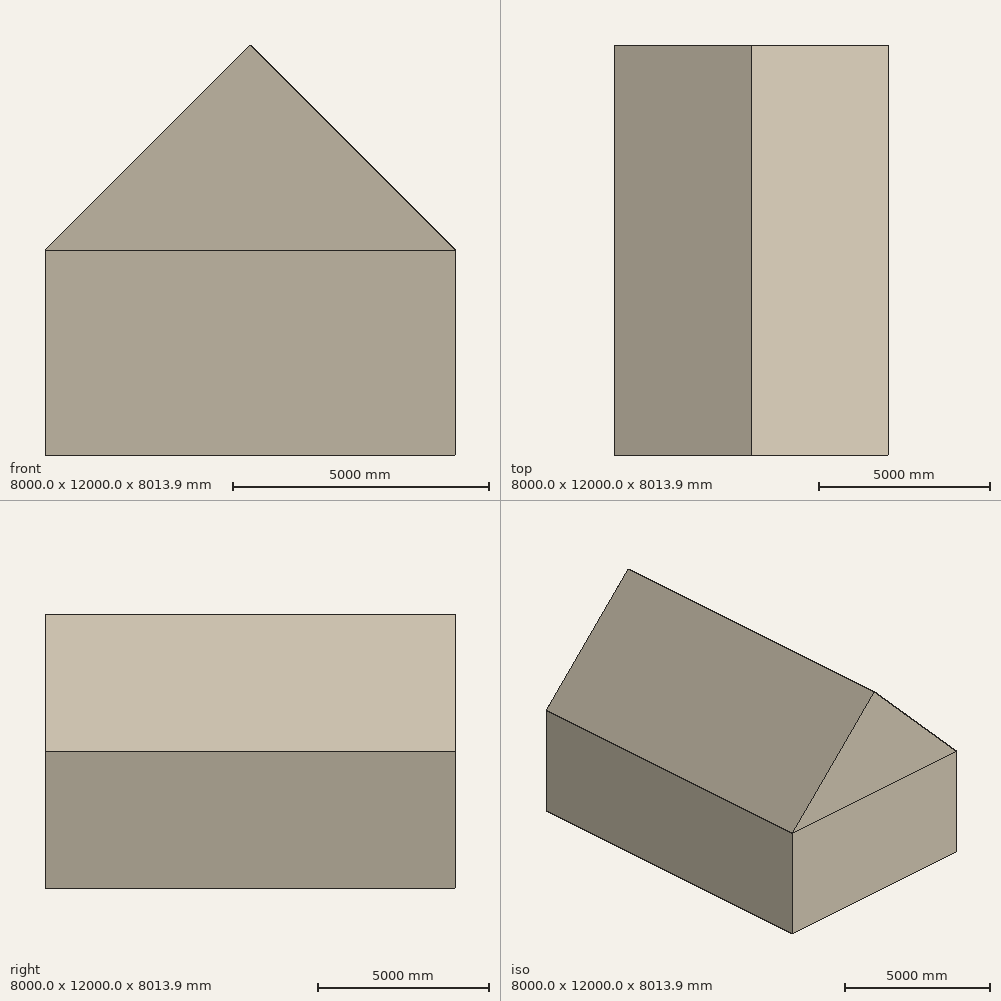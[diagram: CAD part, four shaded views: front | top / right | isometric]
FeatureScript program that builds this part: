
annotation { "Feature Type Name" : "Feature", "Feature Type Description" : "" }
export const myFeature = defineFeature(function(context is Context, id is Id, definition is map)
    precondition{}
    {
        {
            var Q0;
            Q0=qCreatedBy(makeId("Front.planeOp"),FACE);
            var sketch = newSketch(context, id + "F0", { "sketchPlane" : qUnion([Q0])});
            skLineSegment(sketch, "E0.bottom", {"start": v(0, 0) * mm, "end": v(8000, 0) * mm});
            skLineSegment(sketch, "E0.top", {"start": v(0, 4000) * mm, "end": v(8000, 4000) * mm});
            skLineSegment(sketch, "E0.left", {"start": v(0, 0) * mm, "end": v(0, 4000) * mm});
            skLineSegment(sketch, "E0.right", {"start": v(8000, 0) * mm, "end": v(8000, 4000) * mm});
            skSolve(sketch);
        }
        {
            var Q0;
            Q0 = qSketchRegion(id + "F0", true);
            extrude(context, id + "F1", {"entities" : qUnion([Q0]), "depth" : 12000 * mm});
        }
        {
            var Q0;
            Q0=qCreatedBy(makeId("Front.planeOp"),FACE);
            var sketch = newSketch(context, id + "F2", { "sketchPlane" : qUnion([Q0])});
            skLineSegment(sketch, "E1", {"start": v(0, 4013.9) * mm, "end": v(4000, 4013.9) * mm});
            skLineSegment(sketch, "E2", {"start": v(4000, 4013.9) * mm, "end": v(4000, 8013.9) * mm});
            skPoint(sketch, "E2.endSnap0", {"position": v(3969.53, 8013.9) * mm});
            skLineSegment(sketch, "E3", {"start": v(4000, 8013.9) * mm, "end": v(0, 4013.9) * mm});
            skLineSegment(sketch, "E4", {"start": v(4000, 8013.9) * mm, "end": v(8000, 4013.9) * mm});
            skLineSegment(sketch, "E5", {"start": v(8000, 4013.9) * mm, "end": v(4000, 4013.9) * mm});
            skSolve(sketch);
        }
        {
            var Q0;
            Q0=makeQuery(id+"F2.imprint","IMPRINT",FACE,{"disambiguationData":[TD([[makeQuery(id+"F2.imprint","IMPRINT",EDGE,{"derivedFrom":sQuery(id+"F2.wireOp",EDGE,"E2")}),-1.0]])]});
            var Q1;
            Q1=makeQuery(id+"F2.imprint","IMPRINT",FACE,{"disambiguationData":[TD([[makeQuery(id+"F2.imprint","IMPRINT",EDGE,{"derivedFrom":sQuery(id+"F2.wireOp",EDGE,"E1")}),1.0]])]});
            extrude(context, id + "F3", {"entities" : qUnion([Q0, Q1]), "depth" : 12000 * mm});
        }
    });
